# Revit family: HOSPIVAC 2 EVISA
name_source: partatom
category: Equipement de génie climatique
revit_build: Autodesk Revit 2018 (Build: 20170223_1515(x64)
units: mm (PartAtom-declared; Revit-internal decimal feet)

## family parameters
Basée sur le plan de construction = Non
Classification = Aucun
Cote de connecteur circulaire = Utiliser le diamètre
Couper avec des vides une fois chargée = Non
Partagée = Non
Point de calcul de pièce = Non
Toujours verticalement = Oui
Type d'élément = Normal

## types (7) — shared parameters
BRANCHEMENT_TERRE = Oui
COS_PHI = 0.9
DOUBLE_ALIMENTATION = Oui
ENTRAXE_ALIM_ELEC = 526 mm
EP.VIROLE = 3 mm  [stored 0.00984252 ft]
Fabricant = MIL'S
Lien espace client = https://www.mils.fr
Modèle = HOSPIVAC
NBR_POLES = 3
NEUTRE = Oui
OFFSET_SELLETTE_1 = 110 mm  [stored 0.360892 ft]
TENSION_ALIM = 400 V

## per-type parameters (varying)
- e - HOSPIVAC 2 E150.R: DEBIT_ASPI_VIDE=264.0 m³/h; DEBIT_REFOUL_VIDE=264.0 m³/h; DEGAG_CALORIFIQUE(kJ/h)=24805; DESCR_ALIM_X=Alimentation X ; 5G2.5mm²; DESCR_ALIM_Y=Alimentation Y ; 5G2.5mm²; DESCR_ASPI=Aspiration Vide ; 2x132 m³/h ; G 2"FEM; DESCR_REFOUL=Refoulement Vide ; 2x132 m³/h ; G 2"MAL; DIAM_ASPI_VIDE=50 mm  [stored 0.164042 ft]; DIAM_REFOUL_VIDE=50 mm  [stored 0.164042 ft]; ENTRAXE_CANA_ASPI=680 mm; ENTRAXE_SELLETTE=450 mm; HAUTEUR=1560 mm; HAUT_ASPI=1290 mm; HAUT_CANA_FILTRE=40 mm  [stored 0.131234 ft]; HAUT_CANA_REFOUL=1410 mm; HAUT_FILTRE=410 mm; HAUT_REFOUL=1530 mm; HAUT_TETE_FILTRE=104 mm; HAUT_VIROLE=155 mm  [stored 0.50853 ft]; LARGEUR=970 mm; LG_VIROLE=2000 mm; LONGUEUR=2300 mm; LONG_ENTRAXE_PIED=1500 mm; LONG_FOND=145 mm; LONG_OFFSET_REFOUL=230 mm; LONG_SELLETTE_1=510 mm; LONG_SELLETTE_2=400 mm; NIVEAU_SONORE(dB(A))=69; OFFSET1_LARG_ZONE_MAINT=695 mm; OFFSET2_LARG_ZONE_MAINT=625 mm; OFFSET_COUDE_CANA_FILTRE=230 mm; OFFSET_EVISA300=0 mm  [stored 0 ft]; OFFSET_HAUT_FILTRE=750 mm; OFFSET_HAUT_SELLETTE=860 mm; OFFSET_LARG_ASPI_PPE=150 mm; OFFSET_LARG_FILTRE=415 mm; OFFSET_LARG_PPE=496 mm; OFFSET_LARG_REFOUL=309 mm; OFFSET_LONG_CANA_ASPI=414.5 mm; OFFSET_LONG_CANA_REFOUL=1314 mm; OFFSET_LONG_FILTRE1=605 mm; OFFSET_LONG_FILTRE2=40 mm  [stored 0.131234 ft]; OFFSET_LONG_PPE=90 mm  [stored 0.295276 ft]; OFFSET_LONG_PPE_2=940 mm; OFFSET_LONG_REFOUL=221 mm  [stored 0.725066 ft]; POIDS(Kg)=585 mm; PUISS_APPARENTE=3333 VA; PUISS_APPARENTE_2=3333 VA; PUISS_ELECT=3 kW; PUISS_ELECT_2=3 kW; TAILLE_POMPE=EVISA : g - E150.R; ØCANA=50 mm  [stored 0.164042 ft]; ØFILTRE=190 mm  [stored 0.62336 ft]; ØPOT_FILTRE=150 mm; ØVIROLE=650 mm
- f - HOSPIVAC 2 E200.R: DEBIT_ASPI_VIDE=400.0 m³/h; DEBIT_REFOUL_VIDE=400.0 m³/h; DEGAG_CALORIFIQUE(kJ/h)=33074; DESCR_ALIM_X=Alimentation X ; 5G2.5mm²; DESCR_ALIM_Y=Alimentation Y ; 5G2.5mm²; DESCR_ASPI=Aspiration Vide ; 2x200 m³/h ; G 2"FEM; DESCR_REFOUL=Refoulement Vide ; 2x200 m³/h ; G 2"MAL; DIAM_ASPI_VIDE=50 mm  [stored 0.164042 ft]; DIAM_REFOUL_VIDE=50 mm  [stored 0.164042 ft]; ENTRAXE_CANA_ASPI=680 mm; ENTRAXE_SELLETTE=450 mm; HAUTEUR=1560 mm; HAUT_ASPI=1290 mm; HAUT_CANA_FILTRE=30 mm  [stored 0.0984252 ft]; HAUT_CANA_REFOUL=1410 mm; HAUT_FILTRE=410 mm; HAUT_REFOUL=1530 mm; HAUT_TETE_FILTRE=104 mm; HAUT_VIROLE=155 mm  [stored 0.50853 ft]; LARGEUR=970 mm; LG_VIROLE=2000 mm; LONGUEUR=2300 mm; LONG_ENTRAXE_PIED=1500 mm; LONG_FOND=145 mm; LONG_OFFSET_REFOUL=270 mm  [stored 0.885827 ft]; LONG_SELLETTE_1=510 mm; LONG_SELLETTE_2=400 mm; NIVEAU_SONORE(dB(A))=71; OFFSET1_LARG_ZONE_MAINT=690 mm; OFFSET2_LARG_ZONE_MAINT=625 mm; OFFSET_COUDE_CANA_FILTRE=230 mm; OFFSET_EVISA300=0 mm  [stored 0 ft]; OFFSET_HAUT_FILTRE=750 mm; OFFSET_HAUT_SELLETTE=860 mm; OFFSET_LARG_ASPI_PPE=150 mm; OFFSET_LARG_FILTRE=410 mm; OFFSET_LARG_PPE=432 mm; OFFSET_LARG_REFOUL=310.5 mm  [stored 1.0187 ft]; OFFSET_LONG_CANA_ASPI=414.5 mm; OFFSET_LONG_CANA_REFOUL=1314 mm; OFFSET_LONG_FILTRE1=650 mm; OFFSET_LONG_FILTRE2=40 mm  [stored 0.131234 ft]; OFFSET_LONG_PPE=90 mm  [stored 0.295276 ft]; OFFSET_LONG_PPE_2=940 mm; OFFSET_LONG_REFOUL=221 mm  [stored 0.725066 ft]; POIDS(Kg)=565 mm; PUISS_APPARENTE=4444 VA; PUISS_APPARENTE_2=4444 VA; PUISS_ELECT=4 kW; PUISS_ELECT_2=4 kW; TAILLE_POMPE=EVISA : h - E200.R; ØCANA=50 mm  [stored 0.164042 ft]; ØFILTRE=180 mm  [stored 0.590551 ft]; ØPOT_FILTRE=150 mm; ØVIROLE=650 mm
- g - HOSPIVAC 2 E300.R: DEBIT_ASPI_VIDE=600.0 m³/h; DEBIT_REFOUL_VIDE=600.0 m³/h; DEGAG_CALORIFIQUE(kJ/h)=45476; DESCR_ALIM_X=Alimentation X ; 5G2.5mm²; DESCR_ALIM_Y=Alimentation Y ; 5G2.5mm²; DESCR_ASPI=Aspiration Vide ; 2x300 m³/h ; G 2"FEM; DESCR_REFOUL=Refoulement Vide ; 2x300 m³/h ; G 2"MAL; DIAM_ASPI_VIDE=50 mm  [stored 0.164042 ft]; DIAM_REFOUL_VIDE=50 mm  [stored 0.164042 ft]; ENTRAXE_CANA_ASPI=680 mm; ENTRAXE_SELLETTE=450 mm; HAUTEUR=1560 mm; HAUT_ASPI=1290 mm; HAUT_CANA_FILTRE=30 mm  [stored 0.0984252 ft]; HAUT_CANA_REFOUL=1410 mm; HAUT_FILTRE=410 mm; HAUT_REFOUL=1530 mm; HAUT_TETE_FILTRE=104 mm; HAUT_VIROLE=155 mm  [stored 0.50853 ft]; LARGEUR=1070 mm; LG_VIROLE=2000 mm; LONGUEUR=2300 mm; LONG_ENTRAXE_PIED=1500 mm; LONG_FOND=145 mm; LONG_OFFSET_REFOUL=270 mm  [stored 0.885827 ft]; LONG_SELLETTE_1=510 mm; LONG_SELLETTE_2=400 mm; NIVEAU_SONORE(dB(A))=72; OFFSET1_LARG_ZONE_MAINT=690 mm; OFFSET2_LARG_ZONE_MAINT=730 mm; OFFSET_COUDE_CANA_FILTRE=230 mm; OFFSET_EVISA300=105 mm  [stored 0.344488 ft]; OFFSET_HAUT_FILTRE=750 mm; OFFSET_HAUT_SELLETTE=860 mm; OFFSET_LARG_ASPI_PPE=200 mm  [stored 0.656168 ft]; OFFSET_LARG_FILTRE=410 mm; OFFSET_LARG_PPE=530 mm; OFFSET_LARG_REFOUL=321.5 mm; OFFSET_LONG_CANA_ASPI=414.5 mm; OFFSET_LONG_CANA_REFOUL=1314 mm; OFFSET_LONG_FILTRE1=650 mm; OFFSET_LONG_FILTRE2=40 mm  [stored 0.131234 ft]; OFFSET_LONG_PPE=90 mm  [stored 0.295276 ft]; OFFSET_LONG_PPE_2=940 mm; OFFSET_LONG_REFOUL=221 mm  [stored 0.725066 ft]; POIDS(Kg)=600 mm; PUISS_APPARENTE=6111 VA; PUISS_APPARENTE_2=6111 VA; PUISS_ELECT=6 kW; PUISS_ELECT_2=6 kW; TAILLE_POMPE=EVISA : i - E300.R; ØCANA=50 mm  [stored 0.164042 ft]; ØFILTRE=180 mm  [stored 0.590551 ft]; ØPOT_FILTRE=150 mm; ØVIROLE=650 mm
- d - HOSPIVAC 2 E100.R: DEBIT_ASPI_VIDE=200.0 m³/h; DEBIT_REFOUL_VIDE=200.0 m³/h; DEGAG_CALORIFIQUE(kJ/h)=18190; DESCR_ALIM_X=Alimentation X ; 5G1.5mm²; DESCR_ALIM_Y=Alimentation Y ; 5G1.5mm²; DESCR_ASPI=Aspiration Vide ; 2x100 m³/h ; G 1"1/4 FEM; DESCR_REFOUL=Refoulement Vide ; 2x100 m³/h ; G 1"1/4 MAL; DIAM_ASPI_VIDE=32 mm  [stored 0.104987 ft]; DIAM_REFOUL_VIDE=32 mm  [stored 0.104987 ft]; ENTRAXE_CANA_ASPI=680 mm; ENTRAXE_SELLETTE=450 mm; HAUTEUR=1350 mm; HAUT_ASPI=1205 mm; HAUT_CANA_FILTRE=30 mm  [stored 0.0984252 ft]; HAUT_CANA_REFOUL=1225 mm; HAUT_FILTRE=430 mm; HAUT_REFOUL=1315 mm; HAUT_TETE_FILTRE=80 mm  [stored 0.262467 ft]; HAUT_VIROLE=155 mm  [stored 0.50853 ft]; LARGEUR=880 mm; LG_VIROLE=2000 mm; LONGUEUR=2300 mm; LONG_ENTRAXE_PIED=1500 mm; LONG_FOND=145 mm; LONG_OFFSET_REFOUL=119 mm; LONG_SELLETTE_1=510 mm; LONG_SELLETTE_2=400 mm; NIVEAU_SONORE(dB(A))=67; OFFSET1_LARG_ZONE_MAINT=665 mm; OFFSET2_LARG_ZONE_MAINT=616 mm; OFFSET_COUDE_CANA_FILTRE=230 mm; OFFSET_EVISA300=0 mm  [stored 0 ft]; OFFSET_HAUT_FILTRE=733 mm; OFFSET_HAUT_SELLETTE=860 mm; OFFSET_LARG_ASPI_PPE=150 mm; OFFSET_LARG_FILTRE=410 mm; OFFSET_LARG_PPE=350 mm; OFFSET_LARG_REFOUL=312 mm; OFFSET_LONG_CANA_ASPI=414.5 mm; OFFSET_LONG_CANA_REFOUL=1436 mm; OFFSET_LONG_FILTRE1=650 mm; OFFSET_LONG_FILTRE2=40 mm  [stored 0.131234 ft]; OFFSET_LONG_PPE=180 mm  [stored 0.590551 ft]; OFFSET_LONG_PPE_2=1029 mm; OFFSET_LONG_REFOUL=221 mm  [stored 0.725066 ft]; POIDS(Kg)=390 mm; PUISS_APPARENTE=2444 VA; PUISS_APPARENTE_2=2444 VA; PUISS_ELECT=2 kW; PUISS_ELECT_2=2 kW; TAILLE_POMPE=EVISA : f - E100.R; ØCANA=32 mm  [stored 0.104987 ft]; ØFILTRE=130 mm; ØPOT_FILTRE=120 mm; ØVIROLE=650 mm
- c - HOSPIVAC 2 E65.R: DEBIT_ASPI_VIDE=136.0 m³/h; DEBIT_REFOUL_VIDE=136.0 m³/h; DEGAG_CALORIFIQUE(kJ/h)=12403; DESCR_ALIM_X=Alimentation X ; 5G1.5mm²; DESCR_ALIM_Y=Alimentation Y ; 5G1.5mm²; DESCR_ASPI=Aspiration Vide ; 2x68 m³/h ; G 1"1/4 FEM; DESCR_REFOUL=Refoulement Vide ; 2x68 m³/h ; G 1"1/4 MAL; DIAM_ASPI_VIDE=32 mm  [stored 0.104987 ft]; DIAM_REFOUL_VIDE=32 mm  [stored 0.104987 ft]; ENTRAXE_CANA_ASPI=680 mm; ENTRAXE_SELLETTE=450 mm; HAUTEUR=1350 mm; HAUT_ASPI=1205 mm; HAUT_CANA_FILTRE=20 mm  [stored 0.0656168 ft]; HAUT_CANA_REFOUL=1235 mm; HAUT_FILTRE=420 mm; HAUT_REFOUL=1315 mm; HAUT_TETE_FILTRE=104 mm; HAUT_VIROLE=155 mm  [stored 0.50853 ft]; LARGEUR=880 mm; LG_VIROLE=2000 mm; LONGUEUR=2300 mm; LONG_ENTRAXE_PIED=1500 mm; LONG_FOND=145 mm; LONG_OFFSET_REFOUL=200 mm  [stored 0.656168 ft]; LONG_SELLETTE_1=510 mm; LONG_SELLETTE_2=400 mm; NIVEAU_SONORE(dB(A))=67; OFFSET1_LARG_ZONE_MAINT=657.5 mm; OFFSET2_LARG_ZONE_MAINT=616 mm; OFFSET_COUDE_CANA_FILTRE=230 mm; OFFSET_EVISA300=0 mm  [stored 0 ft]; OFFSET_HAUT_FILTRE=720 mm; OFFSET_HAUT_SELLETTE=860 mm; OFFSET_LARG_ASPI_PPE=150 mm; OFFSET_LARG_FILTRE=410 mm; OFFSET_LARG_PPE=340 mm; OFFSET_LARG_REFOUL=273.5 mm; OFFSET_LONG_CANA_ASPI=414.5 mm; OFFSET_LONG_CANA_REFOUL=1437.5 mm; OFFSET_LONG_FILTRE1=650 mm; OFFSET_LONG_FILTRE2=40 mm  [stored 0.131234 ft]; OFFSET_LONG_PPE=180 mm  [stored 0.590551 ft]; OFFSET_LONG_PPE_2=1029 mm; OFFSET_LONG_REFOUL=221 mm  [stored 0.725066 ft]; POIDS(Kg)=385 mm; PUISS_APPARENTE=1667 VA; PUISS_APPARENTE_2=1667 VA; PUISS_ELECT=2 kW; PUISS_ELECT_2=2 kW; TAILLE_POMPE=EVISA : e - E65.R; ØCANA=32 mm  [stored 0.104987 ft]; ØFILTRE=115 mm; ØPOT_FILTRE=100 mm  [stored 0.328084 ft]; ØVIROLE=650 mm
- b- HOSPIVAC 2 E40.R: DEBIT_ASPI_VIDE=88.0 m³/h; DEBIT_REFOUL_VIDE=88.0 m³/h; DEGAG_CALORIFIQUE(kJ/h)=9095; DESCR_ALIM_X=Alimentation X ; 5G1.5mm²; DESCR_ALIM_Y=Alimentation Y ; 5G1.5mm²; DESCR_ASPI=Aspiration Vide ; 2x44 m³/h ; G 1" FEM; DESCR_REFOUL=Refoulement Vide ; 2x44 m³/h ; G 1" MAL; DIAM_ASPI_VIDE=25 mm  [stored 0.082021 ft]; DIAM_REFOUL_VIDE=25 mm  [stored 0.082021 ft]; ENTRAXE_CANA_ASPI=500 mm; ENTRAXE_SELLETTE=420 mm; HAUTEUR=1200 mm; HAUT_ASPI=1085 mm; HAUT_CANA_FILTRE=20 mm  [stored 0.0656168 ft]; HAUT_CANA_REFOUL=1110 mm; HAUT_FILTRE=465 mm; HAUT_REFOUL=1180 mm; HAUT_TETE_FILTRE=60 mm  [stored 0.19685 ft]; HAUT_VIROLE=142 mm  [stored 0.465879 ft]; LARGEUR=830 mm; LG_VIROLE=1490 mm; LONGUEUR=1780 mm; LONG_ENTRAXE_PIED=1180 mm; LONG_FOND=134.5 mm; LONG_OFFSET_REFOUL=150 mm; LONG_SELLETTE_1=405 mm; LONG_SELLETTE_2=310 mm  [stored 1.01706 ft]; NIVEAU_SONORE(dB(A))=58; OFFSET1_LARG_ZONE_MAINT=657 mm; OFFSET2_LARG_ZONE_MAINT=612.5 mm; OFFSET_COUDE_CANA_FILTRE=145 mm; OFFSET_EVISA300=0 mm  [stored 0 ft]; OFFSET_HAUT_FILTRE=640 mm; OFFSET_HAUT_SELLETTE=795 mm; OFFSET_LARG_ASPI_PPE=150 mm; OFFSET_LARG_FILTRE=370 mm; OFFSET_LARG_PPE=211.5 mm; OFFSET_LARG_REFOUL=149 mm; OFFSET_LONG_CANA_ASPI=354.5 mm; OFFSET_LONG_CANA_REFOUL=1234 mm; OFFSET_LONG_FILTRE1=370 mm; OFFSET_LONG_FILTRE2=300 mm  [stored 0.984252 ft]; OFFSET_LONG_PPE=110 mm  [stored 0.360892 ft]; OFFSET_LONG_PPE_2=842 mm; OFFSET_LONG_REFOUL=200 mm  [stored 0.656168 ft]; POIDS(Kg)=250 mm  [stored 0.82021 ft]; PUISS_APPARENTE=1222 VA; PUISS_APPARENTE_2=1222 VA; PUISS_ELECT=1 kW; PUISS_ELECT_2=1 kW; TAILLE_POMPE=EVISA : d - E40.R; ØCANA=25 mm  [stored 0.082021 ft]; ØFILTRE=114 mm; ØPOT_FILTRE=90 mm  [stored 0.295276 ft]; ØVIROLE=600 mm
- a - HOSPIVAC 2 E25.R: DEBIT_ASPI_VIDE=56.0 m³/h; DEBIT_REFOUL_VIDE=56.0 m³/h; DEGAG_CALORIFIQUE(kJ/h)=6201; DESCR_ALIM_X=Alimentation X ; 5G1.5mm²; DESCR_ALIM_Y=Alimentation Y ; 5G1.5mm²; DESCR_ASPI=Aspiration Vide ; 2x28 m³/h ; G 1" FEM; DESCR_REFOUL=Refoulement Vide ; 2x28 m³/h ; G 1" MAL; DIAM_ASPI_VIDE=25 mm  [stored 0.082021 ft]; DIAM_REFOUL_VIDE=25 mm  [stored 0.082021 ft]; ENTRAXE_CANA_ASPI=500 mm; ENTRAXE_SELLETTE=420 mm; HAUTEUR=1200 mm; HAUT_ASPI=1085 mm; HAUT_CANA_FILTRE=20 mm  [stored 0.0656168 ft]; HAUT_CANA_REFOUL=1110 mm; HAUT_FILTRE=465 mm; HAUT_REFOUL=1180 mm; HAUT_TETE_FILTRE=60 mm  [stored 0.19685 ft]; HAUT_VIROLE=142 mm  [stored 0.465879 ft]; LARGEUR=830 mm; LG_VIROLE=1490 mm; LONGUEUR=1780 mm; LONG_ENTRAXE_PIED=1180 mm; LONG_FOND=134.5 mm; LONG_OFFSET_REFOUL=150 mm; LONG_SELLETTE_1=405 mm; LONG_SELLETTE_2=310 mm  [stored 1.01706 ft]; NIVEAU_SONORE(dB(A))=59; OFFSET1_LARG_ZONE_MAINT=657 mm; OFFSET2_LARG_ZONE_MAINT=612.5 mm; OFFSET_COUDE_CANA_FILTRE=145 mm; OFFSET_EVISA300=0 mm  [stored 0 ft]; OFFSET_HAUT_FILTRE=640 mm; OFFSET_HAUT_SELLETTE=795 mm; OFFSET_LARG_ASPI_PPE=150 mm; OFFSET_LARG_FILTRE=370 mm; OFFSET_LARG_PPE=211.5 mm; OFFSET_LARG_REFOUL=149 mm; OFFSET_LONG_CANA_ASPI=354.5 mm; OFFSET_LONG_CANA_REFOUL=1234 mm; OFFSET_LONG_FILTRE1=370 mm; OFFSET_LONG_FILTRE2=300 mm  [stored 0.984252 ft]; OFFSET_LONG_PPE=110 mm  [stored 0.360892 ft]; OFFSET_LONG_PPE_2=842 mm; OFFSET_LONG_REFOUL=200 mm  [stored 0.656168 ft]; POIDS(Kg)=240 mm; PUISS_APPARENTE=833 VA; PUISS_APPARENTE_2=833 VA; PUISS_ELECT=1 kW; PUISS_ELECT_2=1 kW; TAILLE_POMPE=EVISA : b - E25.R; ØCANA=25 mm  [stored 0.082021 ft]; ØFILTRE=114 mm; ØPOT_FILTRE=90 mm  [stored 0.295276 ft]; ØVIROLE=600 mm

note: [stored X ft] marks values corroborated as IEEE doubles in the binary element streams (Revit-internal decimal feet)
